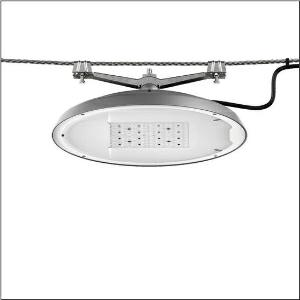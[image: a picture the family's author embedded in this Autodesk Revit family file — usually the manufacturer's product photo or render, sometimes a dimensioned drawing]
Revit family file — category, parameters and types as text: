
# Revit family: dl_r__50_iq_mini___st1_0s_5xa248w41f08me_9ef6
name_source: partatom
category: Lighting Fixtures
units: mm (PartAtom-declared; Revit-internal decimal feet)

## family parameters
Cut with Voids When Loaded = No
Host = Face
Light Source = No
Part Type = Normal
Room Calculation Point = No
Round Connector Dimension = Use Diameter
Shared = No

## types (1)
- --- (1 x LED, 15660 lm, 101.7 W, 4000K)
    Apparent Load = 102 VA
    CIE Flux Codes = 37 72 97 100 100
    Color Rendering = 70
    Color Temperature = 4000K
    Default Elevation = 1800 mm
    Description = DL® 50 iQ mini, catenary luminaire, primary light control with lens, of PMMA, primary optical cover: cover, of toughened safety glass, transparent, light distribution: ST1.0s, light emission: direct distribution, primary light characteristic: symmetric, installation type: suspended mounting, LED, High Power LED, rated luminous flux: 15.660lm, luminous efficacy: 154lm/W, light colour: 740, colour temperature: 4000K, control: optimised constant luminous flux control (CLO 2.0), Desk-Remote (wireless, voltage-free reading and setting of iQ features in the workshop via application-optimized NFC function/RFID function), Light-Fading, Smart-Wire, Night-Set, Lumen-Switch, Temp-Guard, Auto-Match, Street-Remote, mains connection: 230..240V, AC, 50/60Hz, start of lifetime: 102W, end of service life: 111W, reduction: 45W, luminaire housing, of diecast aluminium, powder-coated, Siteco® metallic grey (DB 702S), diameter: 500mm, height: 115mm, protection rating (complete): IP66, insulation class (complete): insulation class II (safety insulation), certification: CE, ENEC, VDE, impact resistance: IK08, permissible operating ambient temperature for outdoor applications: -25..+40°C, standard-compliant lighting for roads and squares, packaging unit: 1 piece

Light Distribution: ST1.0s
    Height = 124 mm  [stored 0.406824 ft]
    Lamp = 1 x LED
    Lamp Light Flux = 15660 lm
    Lamp Power = 101.7 W
    Lamp count = 1
    Length = 500 mm
    Luminous efficacy = 154 lm/W
    Manufacturer = Siteco
    ModVariant = No
    Model = 5XA248W41F08ME
    Number of Poles = 1
    OnlyDefault = Yes
    Power Factor = 1
    Product Name = DL® 50 iQ mini | ST1.0s
    Product group = catenary luminaire
    ProductGroupID = 6300
    Protection Class = Protection class II
    Protection Degree = IP 66
    RLX_Detail_Level = 1
    RLX_Emergency_Light_Flux = 0 lm
    RLX_Emergency_Type = 0
    RLX_Emergency_Type_DB = No
    RlxData = <blob elided: 127421 chars, md5=ed9317dd>
    Socket = socket
    Standby Power = 0 W
    System Light Flux = 15660 lm
    System Power = 102 W
    Type Comments = factory setting: luminous flux: 100 % | dim-lin: 254 | 534 mA
    Type Image = l_1251783.jpg
    URL = http://relux.com
    VarID = @adj_089743
    Voltage = 0 V
    Weight = 0.00 kg
    Width = 0 mm  [stored 0 ft]

note: [stored X ft] marks values corroborated as IEEE doubles in the binary element streams (Revit-internal decimal feet)

## geometry (parser evidence)
native form markers: Blend x4, Sweep x12
no freeform markers — native parametric forms only
